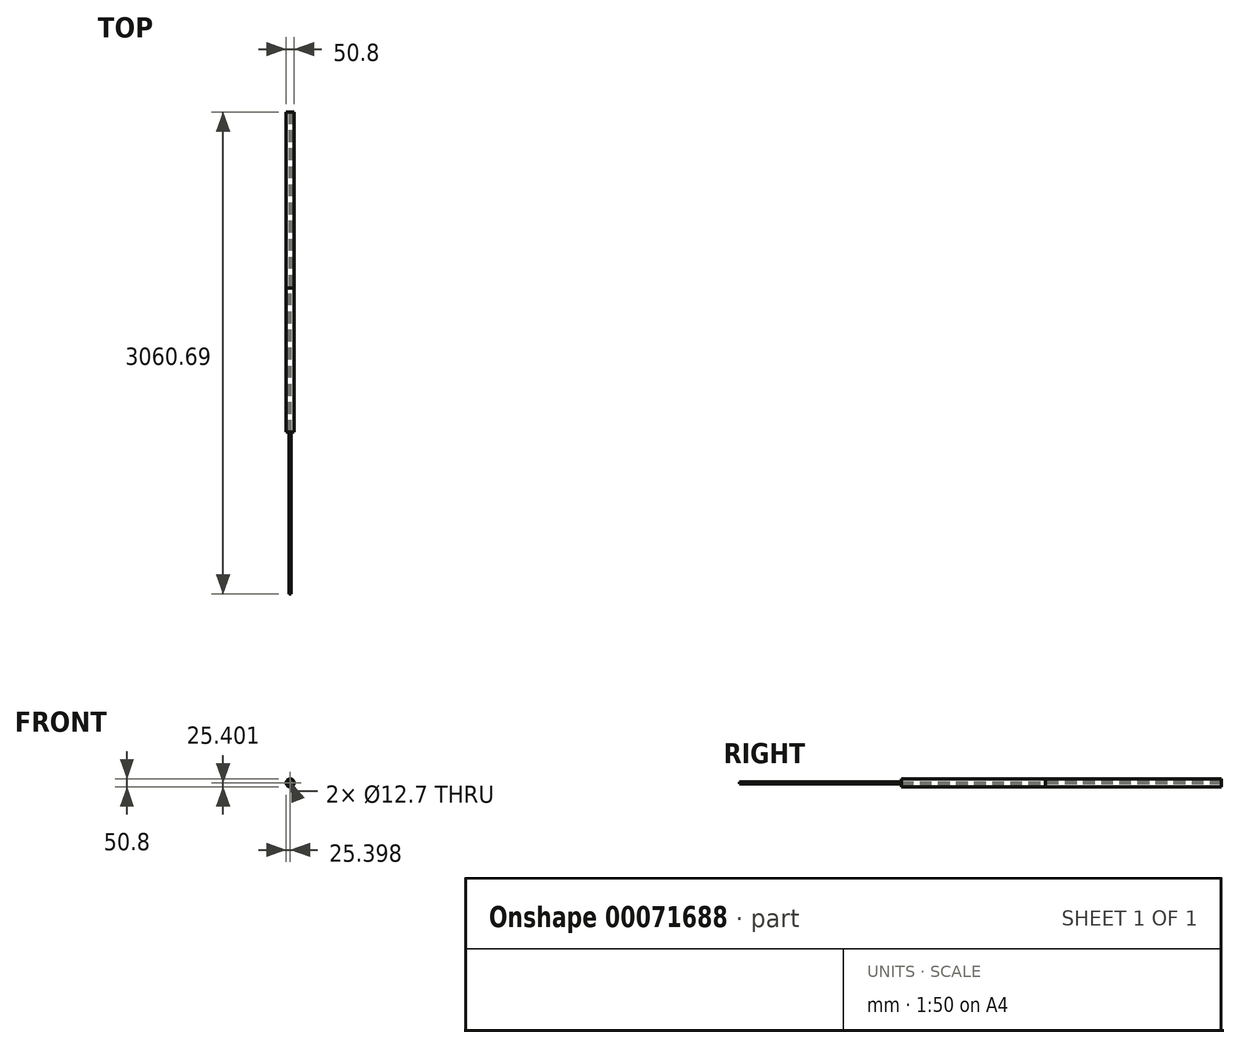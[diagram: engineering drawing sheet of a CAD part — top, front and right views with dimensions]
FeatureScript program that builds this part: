
annotation { "Feature Type Name" : "Feature", "Feature Type Description" : "" }
export const myFeature = defineFeature(function(context is Context, id is Id, definition is map)
    precondition{}
    {
        {
            var Q0;
            Q0=qCreatedBy(makeId("Front.planeOp"),FACE);
            var sketch = newSketch(context, id + "F0", { "sketchPlane" : qUnion([Q0])});
            skCircle(sketch, "E0", {"center": v(-45.46, 36.26) * mm, "radius": 25.4 * mm});
            skSolve(sketch);
        }
        {
            var Q0;
            Q0=makeQuery(id+"F0.imprint","IMPRINT",FACE,{"disambiguationData":[TD([[makeQuery(id+"F0.imprint","IMPRINT",EDGE,{"derivedFrom":sQuery(id+"F0.wireOp",EDGE,"E0")}),1.0]])]});
            extrude(context, id + "F1", {"entities" : qUnion([Q0]), "depth" : 914.4 * mm});
        }
        {
            var Q0;
            Q0=makeQuery(id+"F1.opExtrude","CAP_FACE",FACE,{"disambiguationData":[OSD([sQuery(id+"F0.wireOp",EDGE,"E0")])],"isStart":true});
            var sketch = newSketch(context, id + "F2", { "sketchPlane" : qUnion([Q0])});
            skCircle(sketch, "E1.0", {"center": v(45.46, 36.26) * mm, "radius": 25.4 * mm});
            skCircle(sketch, "E2", {"center": v(45.46, 36.26) * mm, "radius": 6.35 * mm});
            skSolve(sketch);
        }
        {
            var Q0;
            Q0=makeQuery(id+"F1.opExtrude","CAP_FACE",FACE,{"disambiguationData":[OSD([sQuery(id+"F0.wireOp",EDGE,"E0")])],"isStart":false});
            var Q1;
            Q1=makeQuery(id+"F2.imprint","IMPRINT",FACE,{"disambiguationData":[TD([[makeQuery(id+"F2.imprint","IMPRINT",EDGE,{"derivedFrom":sQuery(id+"F2.wireOp",EDGE,"E2")}),1.0]])]});
            extrude(context, id + "F3", {"entities" : qUnion([Q0, Q1]), "operationType" : NewBodyOperationType.REMOVE, "endBound" : BoundingType.THROUGH_ALL, "depth" : 25.4 * mm});
        }
        {
            var Q0;
            Q0=makeQuery(id+"F1.opExtrude","CAP_FACE",FACE,{"disambiguationData":[OSD([sQuery(id+"F0.wireOp",EDGE,"E0")])],"isStart":false});
            var sketch = newSketch(context, id + "F4", { "sketchPlane" : qUnion([Q0])});
            skCircle(sketch, "E3.0", {"center": v(-45.46, 36.26) * mm, "radius": 6.35 * mm});
            skSolve(sketch);
        }
        {
            var Q0;
            Q0=makeQuery(id+"F4.imprint","IMPRINT",FACE,{"disambiguationData":[TD([[makeQuery(id+"F4.imprint","IMPRINT",EDGE,{"derivedFrom":sQuery(id+"F4.wireOp",EDGE,"E3.0")}),1.0]])]});
            extrude(context, id + "F5", {"entities" : qUnion([Q0]), "depth" : 1028.7 * mm});
        }
        {
            var Q0;
            Q0=makeQuery(id+"F1.opExtrude","CAP_FACE",FACE,{"disambiguationData":[OSD([sQuery(id+"F0.wireOp",EDGE,"E0")])],"isStart":true});
            var sketch = newSketch(context, id + "F6", { "sketchPlane" : qUnion([Q0])});
            skCircle(sketch, "E4.0", {"center": v(45.46, 36.26) * mm, "radius": 25.4 * mm});
            skCircle(sketch, "E4.1", {"center": v(45.46, 36.26) * mm, "radius": 6.35 * mm});
            skSolve(sketch);
        }
        {
            var Q0;
            Q0=makeQuery(id+"F6.imprint","IMPRINT",FACE,{"disambiguationData":[TD([[makeQuery(id+"F6.imprint","IMPRINT",EDGE,{"derivedFrom":sQuery(id+"F6.wireOp",EDGE,"E4.0")}),-1.0]])]});
            extrude(context, id + "F7", {"entities" : qUnion([Q0]), "depth" : 1117.6 * mm});
        }
    });
